# Revit family: 06-75-014-DN50-400
name_source: partatom
category: Pipe Accessories
units: mm (PartAtom-declared; Revit-internal decimal feet)

## family parameters
Always vertical = Yes
Cut with Voids When Loaded = No
Part Type = Valve - Breaks Into
Round Connector Dimension = Use Diameter
Shared = No
Work Plane-Based = No

## types (15) — shared parameters
1 = 1 mm  [stored 0.00328084 ft]
DN050_PN16 = 06-050-75-09400992
DN075_PN16 = 06-075-75-09400992
DN080_PN16 = 06-080-75-09400992
DN100_PN16 = 06-100-75-09400992
DN150_PN16 = 06-150-75-09400992
DN200_PN10 = 06-200-75-09400991
DN200_PN16 = 06-200-75-09400992
DN250_PN10 = 06-250-75-09400991
DN250_PN16 = 06-250-75-09400992
DN300_PN10 = 06-300-75-09400871
DN300_PN16 = 06-300-75-09400872
DN350_PN10 = 06-350-75-09400871
DN350_PN16 = 06-350-75-09400872
DN400_PN10 = 06-400-75-09400871
DN400_PN16 = 06-400-75-09400872
Description_ = AVK FLANGED GATE VALVE, PN 10/16
Search_table = 06-75-014-DN50-400
URL_product_pages = https://www.avkvalves.com
zero-valued in all types: Default Elevation

## per-type parameters (varying)
- DN050_PN16: Body_Arc=150 mm; Body_FL_L=67 mm; Body_FL_R=20 mm  [stored 0.0656168 ft]; Body_FL_T=10 mm  [stored 0.0328084 ft]; Body_FL_W=46 mm; Body_FL_arc=200 mm; Body_FL_rib_dim=53 mm; Body_FL_rib_dim1=56 mm; Body_H=110 mm; Body_L=52 mm; Body_R=10 mm  [stored 0.0328084 ft]; Body_T=6 mm  [stored 0.019685 ft]; Body_W=35 mm  [stored 0.114829 ft]; Body_bottom=22 mm  [stored 0.0721785 ft]; Bonnet_dim1=29 mm; Bonnet_dim2=32 mm  [stored 0.104987 ft]; Bonnet_dim3=18 mm  [stored 0.0590551 ft]; Bore_R=25 mm  [stored 0.082021 ft]; DN=50 mm; Dh=125 mm; Ds=19 mm  [stored 0.062336 ft]; F1=7 mm  [stored 0.0229659 ft]; FL_R=83 mm; FL_T=19 mm  [stored 0.062336 ft]; H=83 mm; H3=301 mm; L=150 mm; RIB_L=82 mm; RIB_L1=54 mm; RIB_T=6 mm  [stored 0.019685 ft]; Raised_R=49 mm; Raised_dis=3 mm  [stored 0.00984252 ft]; Rib1_H=60 mm; Rib1_L=80 mm; Rib1_R=20 mm  [stored 0.0656168 ft]; Rib1_T=5 mm  [stored 0.0164042 ft]; Rib1_W=50 mm; Rib2_H=60 mm; Rib2_L=80 mm; Rib2_W=50 mm; Rib3_H=60 mm; Rib3_L=80 mm; Rib3_W=50 mm; Rib4_H=60 mm; Rib4_L=80 mm; Rib4_W=50 mm; Rib5_H=60 mm; Rib5_L=80 mm; Rib5_W=50 mm; Rib_T=16 mm  [stored 0.0524934 ft]; Sweep _cut=2 mm  [stored 0.00656168 ft]; W=83 mm; Wedge_L=30 mm  [stored 0.0984252 ft]; logo_H=55 mm
- DN075_PN16: Body_Arc=206 mm; Body_FL_L=86 mm; Body_FL_R=20 mm  [stored 0.0656168 ft]; Body_FL_T=11 mm  [stored 0.0360892 ft]; Body_FL_W=48 mm; Body_FL_arc=775 mm; Body_FL_rib_dim=70 mm; Body_FL_rib_dim1=71 mm; Body_H=102 mm; Body_L=74 mm; Body_R=15 mm  [stored 0.0492126 ft]; Body_T=6 mm  [stored 0.019685 ft]; Body_W=39 mm  [stored 0.127953 ft]; Body_bottom=44 mm; Bonnet_dim1=36 mm; Bonnet_dim2=34 mm; Bonnet_dim3=21 mm; Bore_R=38 mm  [stored 0.124672 ft]; DN=75 mm; Dh=154 mm; Ds=19 mm  [stored 0.062336 ft]; F1=9 mm  [stored 0.0295276 ft]; FL_R=97 mm; FL_T=19 mm  [stored 0.062336 ft]; H=100 mm; H3=391 mm; L=180 mm; RIB_L=99 mm; RIB_L1=65 mm; RIB_T=6 mm  [stored 0.019685 ft]; Raised_R=64 mm; Raised_dis=3 mm  [stored 0.00984252 ft]; Rib1_H=50 mm; Rib1_L=120 mm; Rib1_R=20 mm  [stored 0.0656168 ft]; Rib1_T=5 mm  [stored 0.0164042 ft]; Rib1_W=60 mm; Rib2_H=50 mm; Rib2_L=120 mm; Rib2_W=60 mm; Rib3_H=50 mm; Rib3_L=120 mm; Rib3_W=60 mm; Rib4_H=50 mm; Rib4_L=120 mm; Rib4_W=60 mm; Rib5_H=50 mm; Rib5_L=120 mm; Rib5_W=60 mm; Rib_T=16 mm  [stored 0.0524934 ft]; Sweep _cut=2 mm  [stored 0.00656168 ft]; W=100 mm; Wedge_L=33 mm; logo_H=51 mm
- DN080_PN16: Body_Arc=212 mm; Body_FL_L=86 mm; Body_FL_R=20 mm  [stored 0.0656168 ft]; Body_FL_T=12 mm  [stored 0.0393701 ft]; Body_FL_W=48 mm; Body_FL_arc=775 mm; Body_FL_rib_dim=70 mm; Body_FL_rib_dim1=71 mm; Body_H=108 mm; Body_L=72 mm; Body_R=16 mm  [stored 0.0524934 ft]; Body_T=7 mm  [stored 0.0229659 ft]; Body_W=35 mm  [stored 0.114829 ft]; Body_bottom=42 mm; Bonnet_dim1=36 mm; Bonnet_dim2=34 mm; Bonnet_dim3=21 mm; Bore_R=40 mm  [stored 0.131234 ft]; DN=80 mm; Dh=160 mm; Ds=19 mm  [stored 0.062336 ft]; F1=9 mm  [stored 0.0295276 ft]; FL_R=100 mm; FL_T=19 mm  [stored 0.062336 ft]; H=100 mm; H3=391 mm; L=180 mm; RIB_L=99 mm; RIB_L1=65 mm; RIB_T=6 mm  [stored 0.019685 ft]; Raised_R=66 mm; Raised_dis=3 mm  [stored 0.00984252 ft]; Rib1_H=58 mm; Rib1_L=120 mm; Rib1_R=20 mm  [stored 0.0656168 ft]; Rib1_T=5 mm  [stored 0.0164042 ft]; Rib1_W=60 mm; Rib2_H=58 mm; Rib2_L=120 mm; Rib2_W=60 mm; Rib3_H=58 mm; Rib3_L=120 mm; Rib3_W=60 mm; Rib4_H=58 mm; Rib4_L=120 mm; Rib4_W=60 mm; Rib5_H=58 mm; Rib5_L=120 mm; Rib5_W=60 mm; Rib_T=16 mm  [stored 0.0524934 ft]; Sweep _cut=2 mm  [stored 0.00656168 ft]; W=100 mm; Wedge_L=30 mm  [stored 0.0984252 ft]; logo_H=54 mm
- DN100_PN16: Body_Arc=220 mm; Body_FL_L=96 mm; Body_FL_R=20 mm  [stored 0.0656168 ft]; Body_FL_T=13 mm; Body_FL_W=53 mm; Body_FL_arc=400 mm; Body_FL_rib_dim=80 mm; Body_FL_rib_dim1=77 mm; Body_H=122 mm; Body_L=82 mm; Body_R=16 mm  [stored 0.0524934 ft]; Body_T=6 mm  [stored 0.019685 ft]; Body_W=38 mm  [stored 0.124672 ft]; Body_bottom=52 mm; Bonnet_dim1=40 mm  [stored 0.131234 ft]; Bonnet_dim2=37 mm; Bonnet_dim3=24 mm  [stored 0.0787402 ft]; Bore_R=50 mm; DN=100 mm; Dh=180 mm; Ds=19 mm  [stored 0.062336 ft]; F1=10 mm  [stored 0.0328084 ft]; FL_R=110 mm; FL_T=18 mm  [stored 0.0590551 ft]; H=110 mm; H3=424 mm; L=190 mm; RIB_L=109 mm; RIB_L1=72 mm; RIB_T=6 mm  [stored 0.019685 ft]; Raised_R=77 mm; Raised_dis=3 mm  [stored 0.00984252 ft]; Rib1_H=72 mm; Rib1_L=120 mm; Rib1_R=20 mm  [stored 0.0656168 ft]; Rib1_T=5 mm  [stored 0.0164042 ft]; Rib1_W=60 mm; Rib2_H=72 mm; Rib2_L=120 mm; Rib2_W=60 mm; Rib3_H=72 mm; Rib3_L=120 mm; Rib3_W=60 mm; Rib4_H=72 mm; Rib4_L=120 mm; Rib4_W=60 mm; Rib5_H=72 mm; Rib5_L=120 mm; Rib5_W=60 mm; Rib_T=15 mm  [stored 0.0492126 ft]; Sweep _cut=2 mm  [stored 0.00656168 ft]; W=110 mm; Wedge_L=32 mm  [stored 0.104987 ft]; logo_H=61 mm
- DN150_PN16: Body_Arc=400 mm; Body_FL_L=136 mm; Body_FL_R=20 mm  [stored 0.0656168 ft]; Body_FL_T=13 mm; Body_FL_W=75 mm; Body_FL_arc=300 mm; Body_FL_rib_dim=113 mm; Body_FL_rib_dim1=87 mm; Body_H=172 mm; Body_L=122 mm; Body_R=16 mm  [stored 0.0524934 ft]; Body_T=6 mm  [stored 0.019685 ft]; Body_W=48 mm; Body_bottom=92 mm; Bonnet_dim1=40 mm  [stored 0.131234 ft]; Bonnet_dim2=53 mm; Bonnet_dim3=24 mm  [stored 0.0787402 ft]; Bore_R=75 mm; DN=150 mm; Dh=240 mm; Ds=23 mm  [stored 0.0754593 ft]; F1=10 mm  [stored 0.0328084 ft]; FL_R=143 mm; FL_T=18 mm  [stored 0.0590551 ft]; H=143 mm; H3=552 mm; L=210 mm; RIB_L=142 mm; RIB_L1=93 mm; RIB_T=6 mm  [stored 0.019685 ft]; Raised_R=106 mm; Raised_dis=3 mm  [stored 0.00984252 ft]; Rib1_H=122 mm; Rib1_L=120 mm; Rib1_R=20 mm  [stored 0.0656168 ft]; Rib1_T=5 mm  [stored 0.0164042 ft]; Rib1_W=60 mm; Rib2_H=122 mm; Rib2_L=120 mm; Rib2_W=60 mm; Rib3_H=122 mm; Rib3_L=120 mm; Rib3_W=60 mm; Rib4_H=122 mm; Rib4_L=120 mm; Rib4_W=60 mm; Rib5_H=122 mm; Rib5_L=120 mm; Rib5_W=60 mm; Rib_T=15 mm  [stored 0.0492126 ft]; Sweep _cut=2 mm  [stored 0.00656168 ft]; W=143 mm; Wedge_L=41 mm; logo_H=86 mm
- DN200_PN10: Body_Arc=500 mm; Body_FL_L=166 mm; Body_FL_R=25 mm  [stored 0.082021 ft]; Body_FL_T=15 mm  [stored 0.0492126 ft]; Body_FL_W=85 mm; Body_FL_arc=450 mm; Body_FL_rib_dim=140 mm; Body_FL_rib_dim1=95 mm; Body_H=220 mm; Body_L=157 mm; Body_R=20 mm  [stored 0.0656168 ft]; Body_T=7 mm  [stored 0.0229659 ft]; Body_W=55 mm; Body_bottom=127 mm; Bonnet_dim1=50 mm; Bonnet_dim2=60 mm; Bonnet_dim3=30 mm  [stored 0.0984252 ft]; Bore_R=100 mm; DN=200 mm; Dh=295 mm; Ds=23 mm  [stored 0.0754593 ft]; F1=12 mm  [stored 0.0393701 ft]; FL_R=170 mm; FL_T=20 mm  [stored 0.0656168 ft]; H=170 mm; H3=669 mm; L=230 mm; RIB_L=169 mm; RIB_L1=111 mm; RIB_T=6 mm  [stored 0.019685 ft]; Raised_R=132 mm; Raised_dis=3 mm  [stored 0.00984252 ft]; Rib1_H=170 mm; Rib1_L=120 mm; Rib1_R=20 mm  [stored 0.0656168 ft]; Rib1_T=5 mm  [stored 0.0164042 ft]; Rib1_W=60 mm; Rib2_H=170 mm; Rib2_L=120 mm; Rib2_W=60 mm; Rib3_H=170 mm; Rib3_L=120 mm; Rib3_W=60 mm; Rib4_H=170 mm; Rib4_L=120 mm; Rib4_W=60 mm; Rib5_H=170 mm; Rib5_L=120 mm; Rib5_W=60 mm; Rib_T=17 mm  [stored 0.0557743 ft]; Sweep _cut=3 mm  [stored 0.00984252 ft]; W=170 mm; Wedge_L=47 mm; logo_H=110 mm
- DN200_PN16: Body_Arc=500 mm; Body_FL_L=166 mm; Body_FL_R=25 mm  [stored 0.082021 ft]; Body_FL_T=15 mm  [stored 0.0492126 ft]; Body_FL_W=85 mm; Body_FL_arc=450 mm; Body_FL_rib_dim=140 mm; Body_FL_rib_dim1=95 mm; Body_H=220 mm; Body_L=157 mm; Body_R=20 mm  [stored 0.0656168 ft]; Body_T=7 mm  [stored 0.0229659 ft]; Body_W=55 mm; Body_bottom=127 mm; Bonnet_dim1=50 mm; Bonnet_dim2=60 mm; Bonnet_dim3=30 mm  [stored 0.0984252 ft]; Bore_R=100 mm; DN=200 mm; Dh=295 mm; Ds=23 mm  [stored 0.0754593 ft]; F1=12 mm  [stored 0.0393701 ft]; FL_R=170 mm; FL_T=20 mm  [stored 0.0656168 ft]; H=170 mm; H3=669 mm; L=230 mm; RIB_L=169 mm; RIB_L1=111 mm; RIB_T=6 mm  [stored 0.019685 ft]; Raised_R=132 mm; Raised_dis=3 mm  [stored 0.00984252 ft]; Rib1_H=170 mm; Rib1_L=120 mm; Rib1_R=20 mm  [stored 0.0656168 ft]; Rib1_T=5 mm  [stored 0.0164042 ft]; Rib1_W=60 mm; Rib2_H=170 mm; Rib2_L=120 mm; Rib2_W=60 mm; Rib3_H=170 mm; Rib3_L=120 mm; Rib3_W=80 mm; Rib4_H=170 mm; Rib4_L=120 mm; Rib4_W=60 mm; Rib5_H=170 mm; Rib5_L=120 mm; Rib5_W=60 mm; Rib_T=17 mm  [stored 0.0557743 ft]; Sweep _cut=3 mm  [stored 0.00984252 ft]; W=170 mm; Wedge_L=47 mm; logo_H=110 mm
- DN250_PN10: Body_Arc=900 mm; Body_FL_L=211 mm; Body_FL_R=25 mm  [stored 0.082021 ft]; Body_FL_T=15 mm  [stored 0.0492126 ft]; Body_FL_W=107 mm; Body_FL_arc=1000 mm; Body_FL_rib_dim=170 mm; Body_FL_rib_dim1=105 mm; Body_H=285 mm; Body_L=196 mm; Body_R=25 mm  [stored 0.082021 ft]; Body_T=9 mm  [stored 0.0295276 ft]; Body_W=73 mm; Body_bottom=166 mm; Bonnet_dim1=57 mm; Bonnet_dim2=75 mm; Bonnet_dim3=34 mm; Bore_R=125 mm; DN=250 mm; Dh=350 mm; Ds=23 mm  [stored 0.0754593 ft]; F1=14 mm  [stored 0.0459318 ft]; FL_R=200 mm; FL_T=20 mm  [stored 0.0656168 ft]; H=200 mm; H3=828 mm; L=250 mm; RIB_L=199 mm; RIB_L1=130 mm; RIB_T=4 mm  [stored 0.0131234 ft]; Raised_R=160 mm; Raised_dis=2 mm  [stored 0.00656168 ft]; Rib1_H=200 mm; Rib1_L=420 mm; Rib1_R=60 mm; Rib1_T=8 mm  [stored 0.0262467 ft]; Rib1_W=195 mm; Rib2_H=160 mm; Rib2_L=200 mm; Rib2_W=140 mm; Rib3_H=220 mm; Rib3_L=200 mm; Rib3_W=140 mm; Rib4_H=180 mm; Rib4_L=200 mm; Rib4_W=140 mm; Rib5_H=220 mm; Rib5_L=200 mm; Rib5_W=140 mm; Rib_T=18 mm  [stored 0.0590551 ft]; Sweep _cut=3 mm  [stored 0.00984252 ft]; W=200 mm; Wedge_L=62 mm; logo_H=143 mm
- DN250_PN16: Body_Arc=900 mm; Body_FL_L=211 mm; Body_FL_R=25 mm  [stored 0.082021 ft]; Body_FL_T=15 mm  [stored 0.0492126 ft]; Body_FL_W=107 mm; Body_FL_arc=1000 mm; Body_FL_rib_dim=170 mm; Body_FL_rib_dim1=105 mm; Body_H=285 mm; Body_L=196 mm; Body_R=25 mm  [stored 0.082021 ft]; Body_T=9 mm  [stored 0.0295276 ft]; Body_W=73 mm; Body_bottom=166 mm; Bonnet_dim1=57 mm; Bonnet_dim2=75 mm; Bonnet_dim3=34 mm; Bore_R=125 mm; DN=250 mm; Dh=355 mm; Ds=28 mm  [stored 0.0918635 ft]; F1=14 mm  [stored 0.0459318 ft]; FL_R=200 mm; FL_T=20 mm  [stored 0.0656168 ft]; H=200 mm; H3=828 mm; L=250 mm; RIB_L=199 mm; RIB_L1=130 mm; RIB_T=4 mm  [stored 0.0131234 ft]; Raised_R=160 mm; Raised_dis=2 mm  [stored 0.00656168 ft]; Rib1_H=200 mm; Rib1_L=420 mm; Rib1_R=60 mm; Rib1_T=8 mm  [stored 0.0262467 ft]; Rib1_W=195 mm; Rib2_H=160 mm; Rib2_L=200 mm; Rib2_W=140 mm; Rib3_H=220 mm; Rib3_L=200 mm; Rib3_W=140 mm; Rib4_H=180 mm; Rib4_L=200 mm; Rib4_W=140 mm; Rib5_H=220 mm; Rib5_L=200 mm; Rib5_W=140 mm; Rib_T=18 mm  [stored 0.0590551 ft]; Sweep _cut=3 mm  [stored 0.00984252 ft]; W=200 mm; Wedge_L=62 mm; logo_H=143 mm
- DN300_PN10: Body_Arc=900 mm; Body_FL_L=228 mm; Body_FL_R=30 mm  [stored 0.0984252 ft]; Body_FL_T=23 mm  [stored 0.0754593 ft]; Body_FL_W=116 mm; Body_FL_arc=1000 mm; Body_FL_rib_dim=198 mm; Body_FL_rib_dim1=115 mm; Body_H=370 mm; Body_L=205 mm; Body_R=30 mm  [stored 0.0984252 ft]; Body_T=9 mm  [stored 0.0295276 ft]; Body_W=85 mm; Body_bottom=175 mm; Bonnet_dim1=57 mm; Bonnet_dim2=81 mm; Bonnet_dim3=34 mm; Bore_R=150 mm; DN=300 mm; Dh=400 mm; Ds=23 mm  [stored 0.0754593 ft]; F1=14 mm  [stored 0.0459318 ft]; FL_R=228 mm; FL_T=20 mm  [stored 0.0656168 ft]; H=228 mm; H3=938 mm; L=270 mm; RIB_L=227 mm; RIB_L1=148 mm; RIB_T=4 mm  [stored 0.0131234 ft]; Raised_R=184 mm; Raised_dis=2 mm  [stored 0.00656168 ft]; Rib1_H=245 mm; Rib1_L=445 mm; Rib1_R=65 mm; Rib1_T=8 mm  [stored 0.0262467 ft]; Rib1_W=230 mm; Rib2_H=170 mm; Rib2_L=200 mm; Rib2_W=180 mm; Rib3_H=190 mm; Rib3_L=200 mm; Rib3_W=180 mm; Rib4_H=200 mm; Rib4_L=200 mm; Rib4_W=180 mm; Rib5_H=170 mm; Rib5_L=445 mm; Rib5_W=230 mm; Rib_T=18 mm  [stored 0.0590551 ft]; Sweep _cut=4 mm  [stored 0.0131234 ft]; W=228 mm; Wedge_L=72 mm; logo_H=185 mm
- DN300_PN16: Body_Arc=900 mm; Body_FL_L=228 mm; Body_FL_R=30 mm  [stored 0.0984252 ft]; Body_FL_T=23 mm  [stored 0.0754593 ft]; Body_FL_W=116 mm; Body_FL_arc=1000 mm; Body_FL_rib_dim=198 mm; Body_FL_rib_dim1=115 mm; Body_H=370 mm; Body_L=205 mm; Body_R=30 mm  [stored 0.0984252 ft]; Body_T=9 mm  [stored 0.0295276 ft]; Body_W=85 mm; Body_bottom=175 mm; Bonnet_dim1=57 mm; Bonnet_dim2=81 mm; Bonnet_dim3=34 mm; Bore_R=150 mm; DN=300 mm; Dh=410 mm; Ds=28 mm  [stored 0.0918635 ft]; F1=14 mm  [stored 0.0459318 ft]; FL_R=228 mm; FL_T=20 mm  [stored 0.0656168 ft]; H=228 mm; H3=938 mm; L=270 mm; RIB_L=227 mm; RIB_L1=148 mm; RIB_T=4 mm  [stored 0.0131234 ft]; Raised_R=184 mm; Raised_dis=2 mm  [stored 0.00656168 ft]; Rib1_H=245 mm; Rib1_L=445 mm; Rib1_R=65 mm; Rib1_T=8 mm  [stored 0.0262467 ft]; Rib1_W=230 mm; Rib2_H=170 mm; Rib2_L=200 mm; Rib2_W=180 mm; Rib3_H=190 mm; Rib3_L=200 mm; Rib3_W=180 mm; Rib4_H=200 mm; Rib4_L=200 mm; Rib4_W=180 mm; Rib5_H=170 mm; Rib5_L=445 mm; Rib5_W=230 mm; Rib_T=18 mm  [stored 0.0590551 ft]; Sweep _cut=4 mm  [stored 0.0131234 ft]; W=228 mm; Wedge_L=72 mm; logo_H=185 mm
- DN350_PN10: Body_Arc=1120 mm; Body_FL_L=282 mm; Body_FL_R=40 mm  [stored 0.131234 ft]; Body_FL_T=28 mm  [stored 0.0918635 ft]; Body_FL_W=125 mm; Body_FL_arc=1550 mm; Body_FL_rib_dim=230 mm; Body_FL_rib_dim1=121 mm; Body_H=485 mm; Body_L=238 mm; Body_R=30 mm  [stored 0.0984252 ft]; Body_T=13 mm; Body_W=86 mm; Body_bottom=208 mm; Bonnet_dim1=67 mm; Bonnet_dim2=88 mm; Bonnet_dim3=40 mm  [stored 0.131234 ft]; Bore_R=175 mm; DN=350 mm; Dh=460 mm; Ds=23 mm  [stored 0.0754593 ft]; F1=16 mm  [stored 0.0524934 ft]; FL_R=520 mm; FL_T=25 mm  [stored 0.082021 ft]; H=260 mm; H3=1184 mm; L=290 mm; RIB_L=259 mm; RIB_L1=169 mm; RIB_T=8 mm  [stored 0.0262467 ft]; Raised_R=215 mm; Raised_dis=4 mm  [stored 0.0131234 ft]; Rib1_H=410 mm; Rib1_L=530 mm; Rib1_R=65 mm; Rib1_T=9 mm  [stored 0.0295276 ft]; Rib1_W=250 mm; Rib2_H=290 mm; Rib2_L=530 mm; Rib2_W=250 mm; Rib3_H=170 mm; Rib3_L=530 mm; Rib3_W=250 mm; Rib4_H=50 mm; Rib4_L=530 mm; Rib4_W=250 mm; Rib5_H=230 mm; Rib5_L=140 mm; Rib5_W=140 mm; Rib_T=21 mm; Sweep _cut=5 mm  [stored 0.0164042 ft]; W=260 mm; Wedge_L=73 mm; logo_H=243 mm
- DN350_PN16: Body_Arc=1120 mm; Body_FL_L=282 mm; Body_FL_R=40 mm  [stored 0.131234 ft]; Body_FL_T=28 mm  [stored 0.0918635 ft]; Body_FL_W=125 mm; Body_FL_arc=1550 mm; Body_FL_rib_dim=230 mm; Body_FL_rib_dim1=121 mm; Body_H=485 mm; Body_L=238 mm; Body_R=30 mm  [stored 0.0984252 ft]; Body_T=13 mm; Body_W=86 mm; Body_bottom=208 mm; Bonnet_dim1=67 mm; Bonnet_dim2=88 mm; Bonnet_dim3=40 mm  [stored 0.131234 ft]; Bore_R=175 mm; DN=350 mm; Dh=470 mm; Ds=28 mm  [stored 0.0918635 ft]; F1=16 mm  [stored 0.0524934 ft]; FL_R=520 mm; FL_T=25 mm  [stored 0.082021 ft]; H=260 mm; H3=1184 mm; L=290 mm; RIB_L=259 mm; RIB_L1=169 mm; RIB_T=8 mm  [stored 0.0262467 ft]; Raised_R=215 mm; Raised_dis=4 mm  [stored 0.0131234 ft]; Rib1_H=410 mm; Rib1_L=530 mm; Rib1_R=65 mm; Rib1_T=9 mm  [stored 0.0295276 ft]; Rib1_W=250 mm; Rib2_H=290 mm; Rib2_L=530 mm; Rib2_W=250 mm; Rib3_H=170 mm; Rib3_L=530 mm; Rib3_W=250 mm; Rib4_H=50 mm; Rib4_L=530 mm; Rib4_W=250 mm; Rib5_H=230 mm; Rib5_L=140 mm; Rib5_W=140 mm; Rib_T=21 mm; Sweep _cut=5 mm  [stored 0.0164042 ft]; W=260 mm; Wedge_L=73 mm; logo_H=243 mm
- DN400_PN10: Body_Arc=1120 mm; Body_FL_L=290 mm; Body_FL_R=50 mm; Body_FL_T=30 mm  [stored 0.0984252 ft]; Body_FL_W=125 mm; Body_FL_arc=1159 mm; Body_FL_rib_dim=260 mm; Body_FL_rib_dim1=131 mm; Body_H=512 mm; Body_L=238 mm; Body_R=30 mm  [stored 0.0984252 ft]; Body_T=13 mm; Body_W=86 mm; Body_bottom=208 mm; Bonnet_dim1=67 mm; Bonnet_dim2=88 mm; Bonnet_dim3=40 mm  [stored 0.131234 ft]; Bore_R=200 mm; DN=400 mm; Dh=515 mm; Ds=28 mm  [stored 0.0918635 ft]; F1=16 mm  [stored 0.0524934 ft]; FL_R=290 mm; FL_T=25 mm  [stored 0.082021 ft]; H=290 mm; H3=1241 mm; L=310 mm; RIB_L=289 mm; RIB_L1=189 mm; RIB_T=8 mm  [stored 0.0262467 ft]; Raised_R=241 mm; Raised_dis=4 mm  [stored 0.0131234 ft]; Rib1_H=430 mm; Rib1_L=564 mm; Rib1_R=70 mm; Rib1_T=10 mm  [stored 0.0328084 ft]; Rib1_W=302 mm; Rib2_H=320 mm; Rib2_L=564 mm; Rib2_W=302 mm; Rib3_H=173 mm; Rib3_L=564 mm; Rib3_W=260 mm; Rib4_H=25 mm  [stored 0.082021 ft]; Rib4_L=564 mm; Rib4_W=260 mm; Rib5_H=230 mm; Rib5_L=150 mm; Rib5_W=150 mm; Rib_T=21 mm; Sweep _cut=5 mm  [stored 0.0164042 ft]; W=290 mm; Wedge_L=73 mm; logo_H=256 mm
- DN400_PN16: Body_Arc=1120 mm; Body_FL_L=290 mm; Body_FL_R=50 mm; Body_FL_T=30 mm  [stored 0.0984252 ft]; Body_FL_W=125 mm; Body_FL_arc=1159 mm; Body_FL_rib_dim=260 mm; Body_FL_rib_dim1=131 mm; Body_H=512 mm; Body_L=238 mm; Body_R=30 mm  [stored 0.0984252 ft]; Body_T=13 mm; Body_W=86 mm; Body_bottom=208 mm; Bonnet_dim1=67 mm; Bonnet_dim2=88 mm; Bonnet_dim3=40 mm  [stored 0.131234 ft]; Bore_R=200 mm; DN=400 mm; Dh=525 mm; Ds=31 mm  [stored 0.101706 ft]; F1=16 mm  [stored 0.0524934 ft]; FL_R=290 mm; FL_T=25 mm  [stored 0.082021 ft]; H=290 mm; H3=1241 mm; L=310 mm; RIB_L=289 mm; RIB_L1=189 mm; RIB_T=8 mm  [stored 0.0262467 ft]; Raised_R=241 mm; Raised_dis=4 mm  [stored 0.0131234 ft]; Rib1_H=430 mm; Rib1_L=564 mm; Rib1_R=70 mm; Rib1_T=10 mm  [stored 0.0328084 ft]; Rib1_W=302 mm; Rib2_H=320 mm; Rib2_L=564 mm; Rib2_W=302 mm; Rib3_H=173 mm; Rib3_L=564 mm; Rib3_W=260 mm; Rib4_H=25 mm  [stored 0.082021 ft]; Rib4_L=564 mm; Rib4_W=260 mm; Rib5_H=230 mm; Rib5_L=150 mm; Rib5_W=150 mm; Rib_T=21 mm; Sweep _cut=5 mm  [stored 0.0164042 ft]; W=290 mm; Wedge_L=73 mm; logo_H=256 mm

note: [stored X ft] marks values corroborated as IEEE doubles in the binary element streams (Revit-internal decimal feet)

## geometry (parser evidence)
native form markers: Sweep x6
no freeform markers — native parametric forms only
